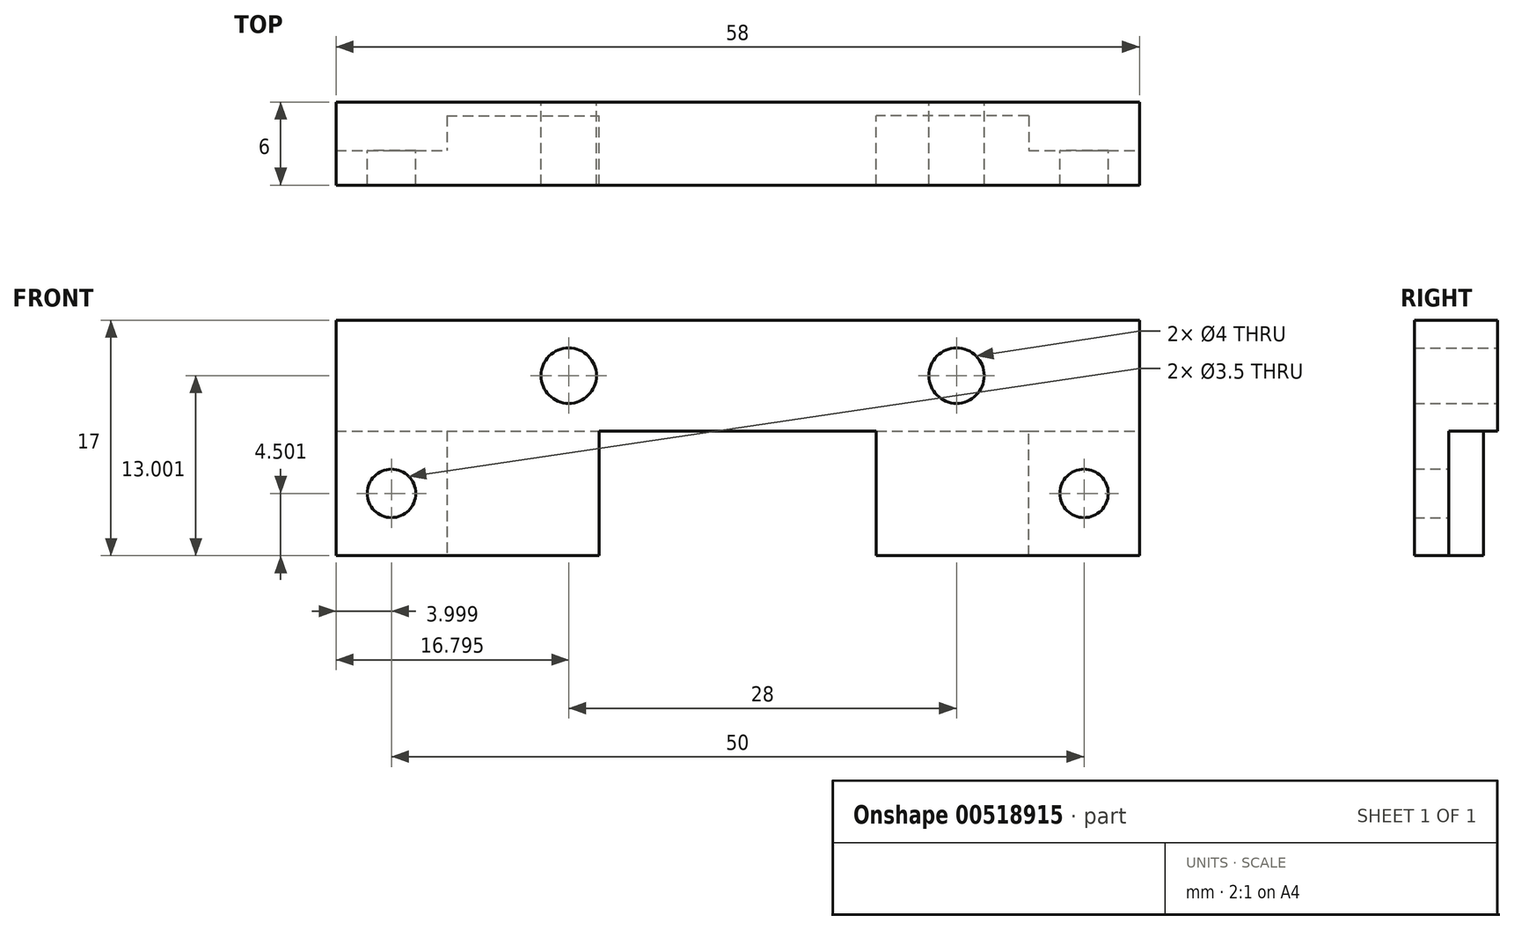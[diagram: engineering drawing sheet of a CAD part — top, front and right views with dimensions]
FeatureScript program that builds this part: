
annotation { "Feature Type Name" : "Feature", "Feature Type Description" : "" }
export const myFeature = defineFeature(function(context is Context, id is Id, definition is map)
    precondition{}
    {
        {
            var Q0;
            Q0=qCreatedBy(makeId("Front.planeOp"),FACE);
            var sketch = newSketch(context, id + "F0", { "sketchPlane" : qUnion([Q0])});
            skLineSegment(sketch, "E0.bottom", {"start": v(-62.01, 20.63) * mm, "end": v(-4.01, 20.63) * mm});
            skLineSegment(sketch, "E0.left", {"start": v(-62.01, 20.63) * mm, "end": v(-62.01, 11.63) * mm});
            skLineSegment(sketch, "E0.right", {"start": v(-4.01, 20.63) * mm, "end": v(-4.01, 11.63) * mm});
            skCircle(sketch, "E1", {"center": v(-58.01, 16.13) * mm, "radius": 1.75 * mm});
            skCircle(sketch, "E2", {"center": v(-8.01, 16.13) * mm, "radius": 1.75 * mm});
            skLineSegment(sketch, "E3", {"start": v(-58.01, 16.13) * mm, "end": v(-33.01, 16.13) * mm, "construction": true});
            skLineSegment(sketch, "E4", {"start": v(-33.01, 16.13) * mm, "end": v(-8.01, 16.13) * mm, "construction": true});
            skLineSegment(sketch, "E5", {"start": v(-33.01, 16.13) * mm, "end": v(-33.01, 20.63) * mm, "construction": true});
            skPoint(sketch, "E5.endSnap0", {"position": v(-33.01, 20.63) * mm});
            skLineSegment(sketch, "E6", {"start": v(-4.01, 20.63) * mm, "end": v(-4.01, 28.63) * mm});
            skLineSegment(sketch, "E7", {"start": v(-4.01, 28.63) * mm, "end": v(-62.01, 28.63) * mm});
            skLineSegment(sketch, "E8", {"start": v(-62.01, 28.63) * mm, "end": v(-62.01, 20.63) * mm});
            skLineSegment(sketch, "E9", {"start": v(-4.01, 11.63) * mm, "end": v(-12.01, 11.63) * mm});
            skLineSegment(sketch, "E10", {"start": v(-12.01, 11.63) * mm, "end": v(-12.01, 20.63) * mm});
            skLineSegment(sketch, "E11", {"start": v(-12.01, 20.63) * mm, "end": v(-54.01, 20.63) * mm});
            skLineSegment(sketch, "E12", {"start": v(-54.01, 20.63) * mm, "end": v(-54.01, 11.63) * mm});
            skLineSegment(sketch, "E13", {"start": v(-54.01, 11.63) * mm, "end": v(-62.01, 11.63) * mm});
            skCircle(sketch, "E14", {"center": v(-17.22, 24.63) * mm, "radius": 2 * mm});
            skCircle(sketch, "E15", {"center": v(-45.22, 24.63) * mm, "radius": 2 * mm});
            skLineSegment(sketch, "E16", {"start": v(-12.01, 11.63) * mm, "end": v(-23.01, 11.63) * mm});
            skLineSegment(sketch, "E17", {"start": v(-23.01, 11.63) * mm, "end": v(-23.01, 20.63) * mm});
            skLineSegment(sketch, "E18", {"start": v(-54.01, 11.63) * mm, "end": v(-43.01, 11.63) * mm});
            skLineSegment(sketch, "E19", {"start": v(-43.01, 11.63) * mm, "end": v(-43.01, 20.63) * mm});
            skSolve(sketch);
        }
        {
            var Q0;
            Q0 = qSketchRegion(id + "F0", true);
            extrude(context, id + "F1", {"entities" : qUnion([Q0]), "depth" : 2.5 * mm, "offsetDistance" : 25 * mm});
        }
        {
            var Q0;
            {var subQ0=sQuery(id+"F0.wireOp",EDGE,"E12");Q0=makeQuery(id+"F0.imprint","IMPRINT",FACE,{"disambiguationData":[TD([[makeQuery(id+"F0.imprint","IMPRINT",EDGE,{"derivedFrom":subQ0}),1.0]])]});}
            var Q1;
            {var subQ0=sQuery(id+"F0.wireOp",EDGE,"E10");Q1=makeQuery(id+"F0.imprint","IMPRINT",FACE,{"disambiguationData":[TD([[makeQuery(id+"F0.imprint","IMPRINT",EDGE,{"derivedFrom":subQ0}),1.0]])]});}
            extrude(context, id + "F2", {"entities" : qUnion([Q0, Q1]), "operationType" : NewBodyOperationType.ADD, "oppositeDirection" : true, "depth" : 2.5 * mm, "offsetDistance" : 25 * mm});
        }
        {
            var Q0;
            {var subQ0=sQuery(id+"F0.wireOp",EDGE,"E6");Q0=makeQuery(id+"F0.imprint","IMPRINT",FACE,{"disambiguationData":[TD([[makeQuery(id+"F0.imprint","IMPRINT",EDGE,{"derivedFrom":subQ0}),1.0]])]});}
            extrude(context, id + "F3", {"entities" : qUnion([Q0]), "operationType" : NewBodyOperationType.ADD, "oppositeDirection" : true, "depth" : 3.5 * mm, "offsetDistance" : 25 * mm});
        }
    });
